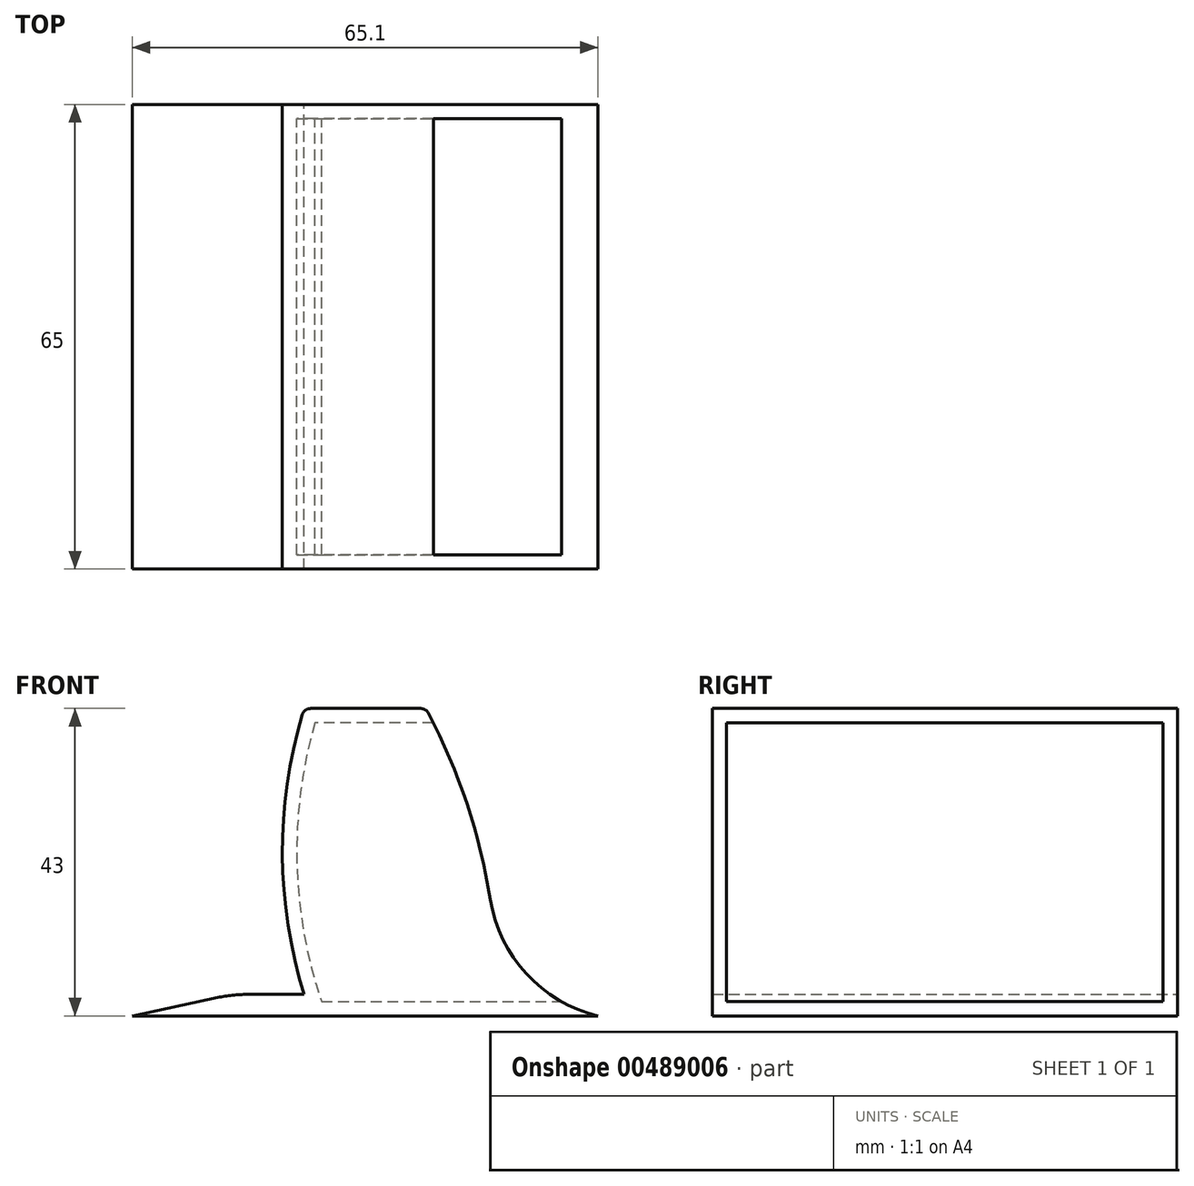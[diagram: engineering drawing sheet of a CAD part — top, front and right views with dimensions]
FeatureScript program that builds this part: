
annotation { "Feature Type Name" : "Feature", "Feature Type Description" : "" }
export const myFeature = defineFeature(function(context is Context, id is Id, definition is map)
    precondition{}
    {
        {
            var Q0;
            Q0=qCreatedBy(makeId("Front.planeOp"),FACE);
            var sketch = newSketch(context, id + "F0", { "sketchPlane" : qUnion([Q0])});
            skLineSegment(sketch, "E0.bottom", {"start": v(11.55, -20) * mm, "end": v(11.55, 20) * mm, "construction": true});
            skLineSegment(sketch, "E0.top", {"start": v(-11.55, -20) * mm, "end": v(-11.55, 20) * mm, "construction": true});
            skLineSegment(sketch, "E0.left", {"start": v(11.55, -20) * mm, "end": v(-11.55, -20) * mm, "construction": true});
            skLineSegment(sketch, "E0.right", {"start": v(11.55, 20) * mm, "end": v(-11.55, 20) * mm, "construction": true});
            skPoint(sketch, "E0.middle", {"position": v(0, 0) * mm});
            skLineSegment(sketch, "E1", {"start": v(-11.55, 0) * mm, "end": v(11.55, 0) * mm, "construction": true});
            skLineSegment(sketch, "E2", {"start": v(0, 20) * mm, "end": v(0, -20) * mm, "construction": true});
            skLineSegment(sketch, "E3", {"start": v(8.5, 20) * mm, "end": v(-8.5, 20) * mm});
            skArc(sketch, "E4", {"start": v(8.5, -20) * mm, "mid": v(11.55, 0) * mm, "end": v(8.5, 20) * mm});
            skLineSegment(sketch, "E5.MirrorCS", {"start": v(8.5, -20) * mm, "end": v(-8.5, -20) * mm});
            skArc(sketch, "E6.MirrorCS", {"start": v(-8.5, -20) * mm, "mid": v(-11.55, 0) * mm, "end": v(-8.5, 20) * mm});
            skArc(sketch, "E7", {"start": v(18.55, -20) * mm, "mid": v(16, 0.62) * mm, "end": v(8.5, 20) * mm});
            skLineSegment(sketch, "E8", {"start": v(8.5, -20) * mm, "end": v(18.55, -20) * mm});
            skLineSegment(sketch, "E9", {"start": v(18.55, -20) * mm, "end": v(32.55, -23) * mm});
            skLineSegment(sketch, "E10", {"start": v(32.55, -23) * mm, "end": v(0, -23) * mm});
            skLineSegment(sketch, "E11.MirrorCS", {"start": v(-32.55, -23) * mm, "end": v(0, -23) * mm});
            skLineSegment(sketch, "E12.MirrorCS", {"start": v(-18.55, -20) * mm, "end": v(-32.55, -23) * mm});
            skLineSegment(sketch, "E13.MirrorCS", {"start": v(-8.5, -20) * mm, "end": v(-18.55, -20) * mm});
            skArc(sketch, "E14.MirrorCS", {"start": v(-18.55, -20) * mm, "mid": v(-16, 0.62) * mm, "end": v(-8.5, 20) * mm});
            skSolve(sketch);
        }
        {
            var Q0;
            Q0=makeQuery(id+"F0.imprint","IMPRINT",FACE,{"disambiguationData":[TD([[makeQuery(id+"F0.imprint","IMPRINT",EDGE,{"derivedFrom":sQuery(id+"F0.wireOp",EDGE,"E4")}),-1.0]])]});
            var Q1;
            Q1=makeQuery(id+"F0.imprint","IMPRINT",FACE,{"disambiguationData":[TD([[makeQuery(id+"F0.imprint","IMPRINT",EDGE,{"derivedFrom":sQuery(id+"F0.wireOp",EDGE,"E6.MirrorCS")}),1.0]])]});
            var Q2;
            Q2=makeQuery(id+"F0.imprint","IMPRINT",FACE,{"disambiguationData":[TD([[makeQuery(id+"F0.imprint","IMPRINT",EDGE,{"derivedFrom":sQuery(id+"F0.wireOp",EDGE,"E5.MirrorCS")}),1.0]])]});
            extrude(context, id + "F1", {"entities" : qUnion([Q0, Q1, Q2]), "depth" : 65 * mm});
        }
        {
            var Q0;
            Q0=makeQuery(id+"F1.opExtrude","SWEPT_EDGE",EDGE,{"disambiguationData":[OSD([sQuery(id+"F0.wireOp",EDGE,"E12.MirrorCS"),sQuery(id+"F0.wireOp",EDGE,"E13.MirrorCS"),sQuery(id+"F0.wireOp",EDGE,"E14.MirrorCS")])]});
            var Q1;
            Q1=makeQuery(id+"F1.opExtrude","SWEPT_EDGE",EDGE,{"disambiguationData":[OSD([sQuery(id+"F0.wireOp",EDGE,"E7"),sQuery(id+"F0.wireOp",EDGE,"E8"),sQuery(id+"F0.wireOp",EDGE,"E9")])]});
            fillet(context, id + "F2", {"entities" : qUnion([Q0, Q1]), "radius" : 20 * mm, "tangentPropagation" : true, "allowEdgeOverflow" : false});
        }
        {
            var Q0;
            Q0=makeQuery(id+"F2.opFillet","BLEND_FACE",FACE,{"disambiguationData":[OSD([sQuery(id+"F0.wireOp",EDGE,"E12.MirrorCS"),sQuery(id+"F0.wireOp",EDGE,"E13.MirrorCS"),sQuery(id+"F0.wireOp",EDGE,"E14.MirrorCS")])]});
            var Q1;
            Q1=makeQuery(id+"F1.opExtrude","SWEPT_FACE",FACE,{"disambiguationData":[OSD([sQuery(id+"F0.wireOp",EDGE,"E14.MirrorCS")])]});
            var Q2;
            Q2=makeQuery(id+"F2.opFillet","BLEND_FACE",FACE,{"disambiguationData":[OSD([sQuery(id+"F0.wireOp",EDGE,"E7"),sQuery(id+"F0.wireOp",EDGE,"E8"),sQuery(id+"F0.wireOp",EDGE,"E9")])]});
            var Q3;
            Q3=makeQuery(id+"F1.opExtrude","SWEPT_FACE",FACE,{"disambiguationData":[OSD([sQuery(id+"F0.wireOp",EDGE,"E7")])]});
            shell(context, id + "F3", {"entities" : qUnion([Q0, Q1, Q2, Q3]), "thickness" : 2 * mm});
        }
        {
            var Q0;
            Q0=makeQuery(id+"F1.opExtrude","SWEPT_EDGE",EDGE,{"disambiguationData":[OSD([sQuery(id+"F0.wireOp",EDGE,"E3"),sQuery(id+"F0.wireOp",EDGE,"E6.MirrorCS"),sQuery(id+"F0.wireOp",EDGE,"E14.MirrorCS")])]});
            var Q1;
            Q1=makeQuery(id+"F1.opExtrude","SWEPT_EDGE",EDGE,{"disambiguationData":[OSD([sQuery(id+"F0.wireOp",EDGE,"E3"),sQuery(id+"F0.wireOp",EDGE,"E4"),sQuery(id+"F0.wireOp",EDGE,"E7")])]});
            fillet(context, id + "F4", {"entities" : qUnion([Q0, Q1]), "radius" : 1.2 * mm, "tangentPropagation" : true, "allowEdgeOverflow" : false});
        }
    });
